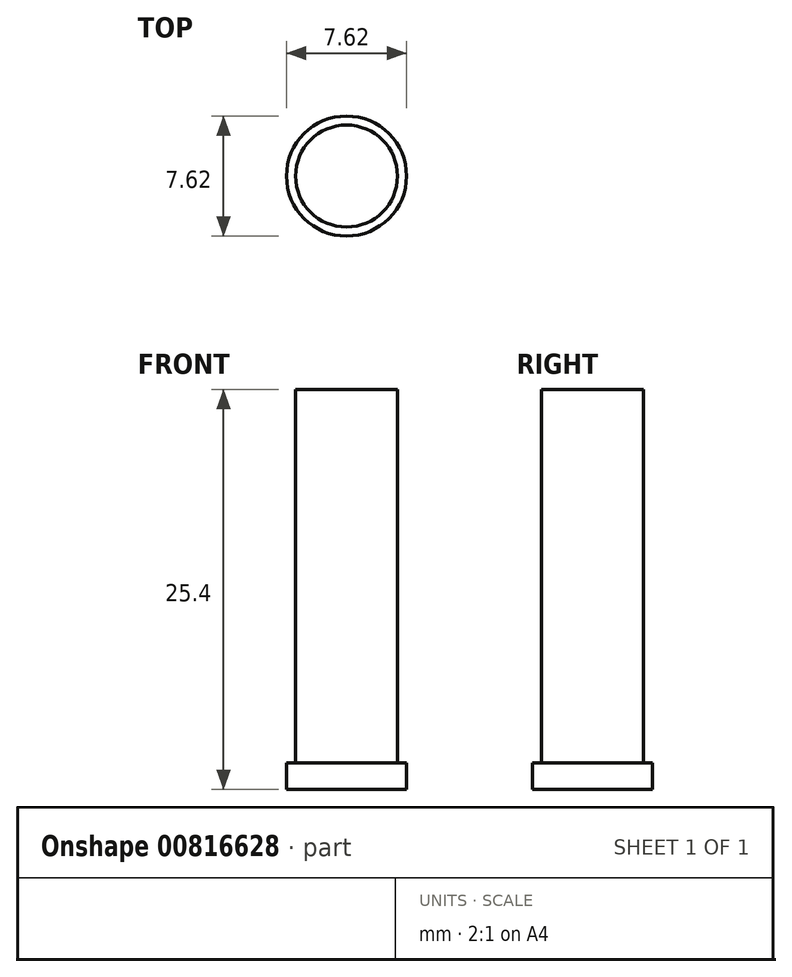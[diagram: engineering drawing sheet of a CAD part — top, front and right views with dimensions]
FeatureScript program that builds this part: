
annotation { "Feature Type Name" : "Feature", "Feature Type Description" : "" }
export const myFeature = defineFeature(function(context is Context, id is Id, definition is map)
    precondition{}
    {
        {
            var Q0;
            Q0=qCreatedBy(makeId("Front.planeOp"),FACE);
            var sketch = newSketch(context, id + "F0", { "sketchPlane" : qUnion([Q0])});
            skLineSegment(sketch, "E0", {"start": v(0, 0) * mm, "end": v(0, 25.4) * mm});
            skLineSegment(sketch, "E1", {"start": v(0, 25.4) * mm, "end": v(3.24, 25.4) * mm});
            skLineSegment(sketch, "E2", {"start": v(3.24, 25.4) * mm, "end": v(3.24, 1.7) * mm});
            skLineSegment(sketch, "E3", {"start": v(3.24, 1.7) * mm, "end": v(3.81, 1.7) * mm});
            skLineSegment(sketch, "E4", {"start": v(3.81, 1.7) * mm, "end": v(3.81, 0) * mm});
            skLineSegment(sketch, "E5", {"start": v(3.81, 0) * mm, "end": v(0, 0) * mm});
            skLineSegment(sketch, "E6", {"start": v(0, 0) * mm, "end": v(0, 32.13) * mm, "construction": true});
            skSolve(sketch);
        }
        {
            var Q0;
            Q0=makeQuery(id+"F0.imprint","IMPRINT",FACE,{"disambiguationData":[TD([[makeQuery(id+"F0.imprint","IMPRINT",EDGE,{"derivedFrom":sQuery(id+"F0.wireOp",EDGE,"E0")}),-1.0]])]});
            var Q1;
            Q1=sQuery(id+"F0.wireOp",EDGE,"E6");
            revolve(context, id + "F1", {"surfaceOperationType" : NewSurfaceOperationType.NEW, "entities" : qUnion([Q0]), "axis" : qUnion([Q1]), "revolveType" : RevolveType.FULL});
        }
    });
